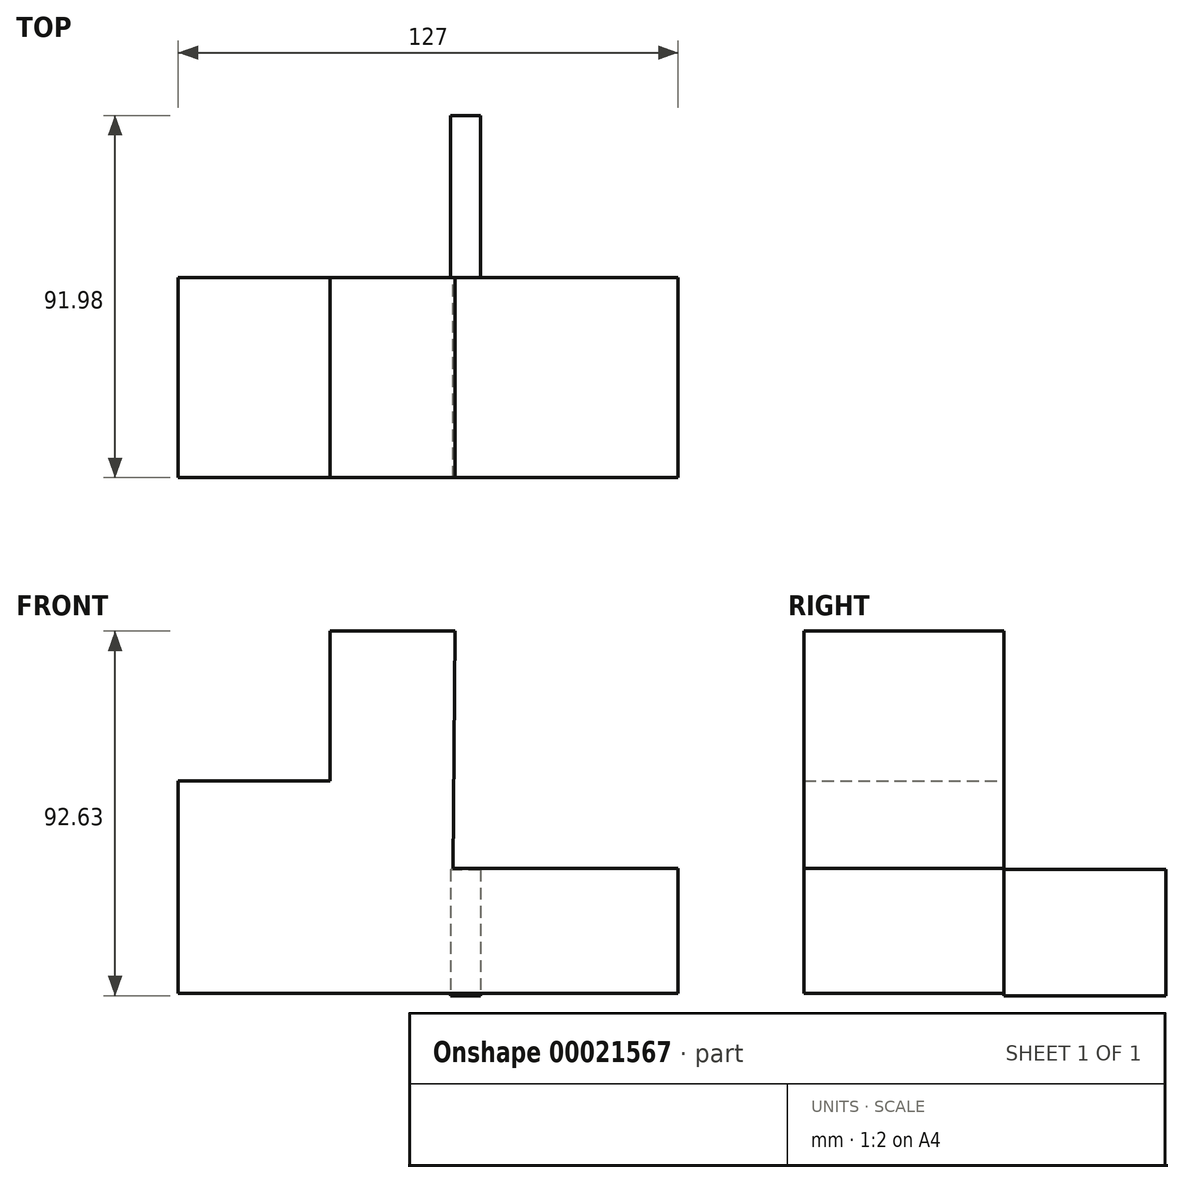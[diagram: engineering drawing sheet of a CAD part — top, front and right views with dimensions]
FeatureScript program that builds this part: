
annotation { "Feature Type Name" : "Feature", "Feature Type Description" : "" }
export const myFeature = defineFeature(function(context is Context, id is Id, definition is map)
    precondition{}
    {
        {
            var Q0;
            Q0=qCreatedBy(makeId("Front.planeOp"),FACE);
            var sketch = newSketch(context, id + "F0", { "sketchPlane" : qUnion([Q0])});
            skLineSegment(sketch, "E0", {"start": v(-76.78, -11.13) * mm, "end": v(-76.78, -65.1) * mm});
            skLineSegment(sketch, "E1", {"start": v(-76.78, -65.1) * mm, "end": v(50.22, -65.1) * mm});
            skLineSegment(sketch, "E2", {"start": v(50.22, -65.1) * mm, "end": v(50.22, -33.36) * mm});
            skLineSegment(sketch, "E3", {"start": v(50.22, -33.36) * mm, "end": v(-6.93, -33.36) * mm});
            skLineSegment(sketch, "E4", {"start": v(-76.78, -11.13) * mm, "end": v(-38.25, -11.13) * mm});
            skLineSegment(sketch, "E5", {"start": v(-38.25, -11.13) * mm, "end": v(-38.25, 26.97) * mm});
            skLineSegment(sketch, "E6", {"start": v(-38.25, 26.97) * mm, "end": v(-6.5, 26.97) * mm});
            skLineSegment(sketch, "E7", {"start": v(-6.5, 26.97) * mm, "end": v(-6.93, -33.36) * mm});
            skSolve(sketch);
        }
        {
            var Q0;
            Q0=makeQuery(id+"F0.imprint","IMPRINT",FACE,{"disambiguationData":[TD([[makeQuery(id+"F0.imprint","IMPRINT",EDGE,{"derivedFrom":sQuery(id+"F0.wireOp",EDGE,"E0")}),1.0]])]});
            extrude(context, id + "F1", {"entities" : qUnion([Q0]), "depth" : 50.8 * mm});
        }
        {
            var Q0;
            Q0=qCreatedBy(makeId("Right.planeOp"),FACE);
            var sketch = newSketch(context, id + "F2", { "sketchPlane" : qUnion([Q0])});
            skLineSegment(sketch, "E8", {"start": v(0, 27.1) * mm, "end": v(0, 10.56) * mm});
            skLineSegment(sketch, "E9", {"start": v(0, 10.56) * mm, "end": v(-19.05, 10.56) * mm});
            skLineSegment(sketch, "E10", {"start": v(-19.05, 27.38) * mm, "end": v(-19.05, 10.56) * mm});
            skLineSegment(sketch, "E11", {"start": v(0, -33.64) * mm, "end": v(41.18, -33.64) * mm});
            skLineSegment(sketch, "E12", {"start": v(41.18, -33.64) * mm, "end": v(41.18, -65.66) * mm});
            skLineSegment(sketch, "E13", {"start": v(41.18, -65.66) * mm, "end": v(0, -65.66) * mm});
            skLineSegment(sketch, "E14", {"start": v(0, -33.64) * mm, "end": v(0, -65.66) * mm});
            skLineSegment(sketch, "E15", {"start": v(0, 10.56) * mm, "end": v(41.29, 10.56) * mm});
            skLineSegment(sketch, "E16", {"start": v(41.29, 10.56) * mm, "end": v(41.18, -33.64) * mm});
            skSolve(sketch);
        }
        {
            var Q0;
            Q0=makeQuery(id+"F2.imprint","IMPRINT",FACE,{"disambiguationData":[TD([[makeQuery(id+"F2.imprint","IMPRINT",EDGE,{"derivedFrom":sQuery(id+"F2.wireOp",EDGE,"E11")}),-1.0]])]});
            extrude(context, id + "F3", {"entities" : qUnion([Q0]), "operationType" : NewBodyOperationType.ADD, "oppositeDirection" : true, "depth" : 7.62 * mm});
        }
    });
